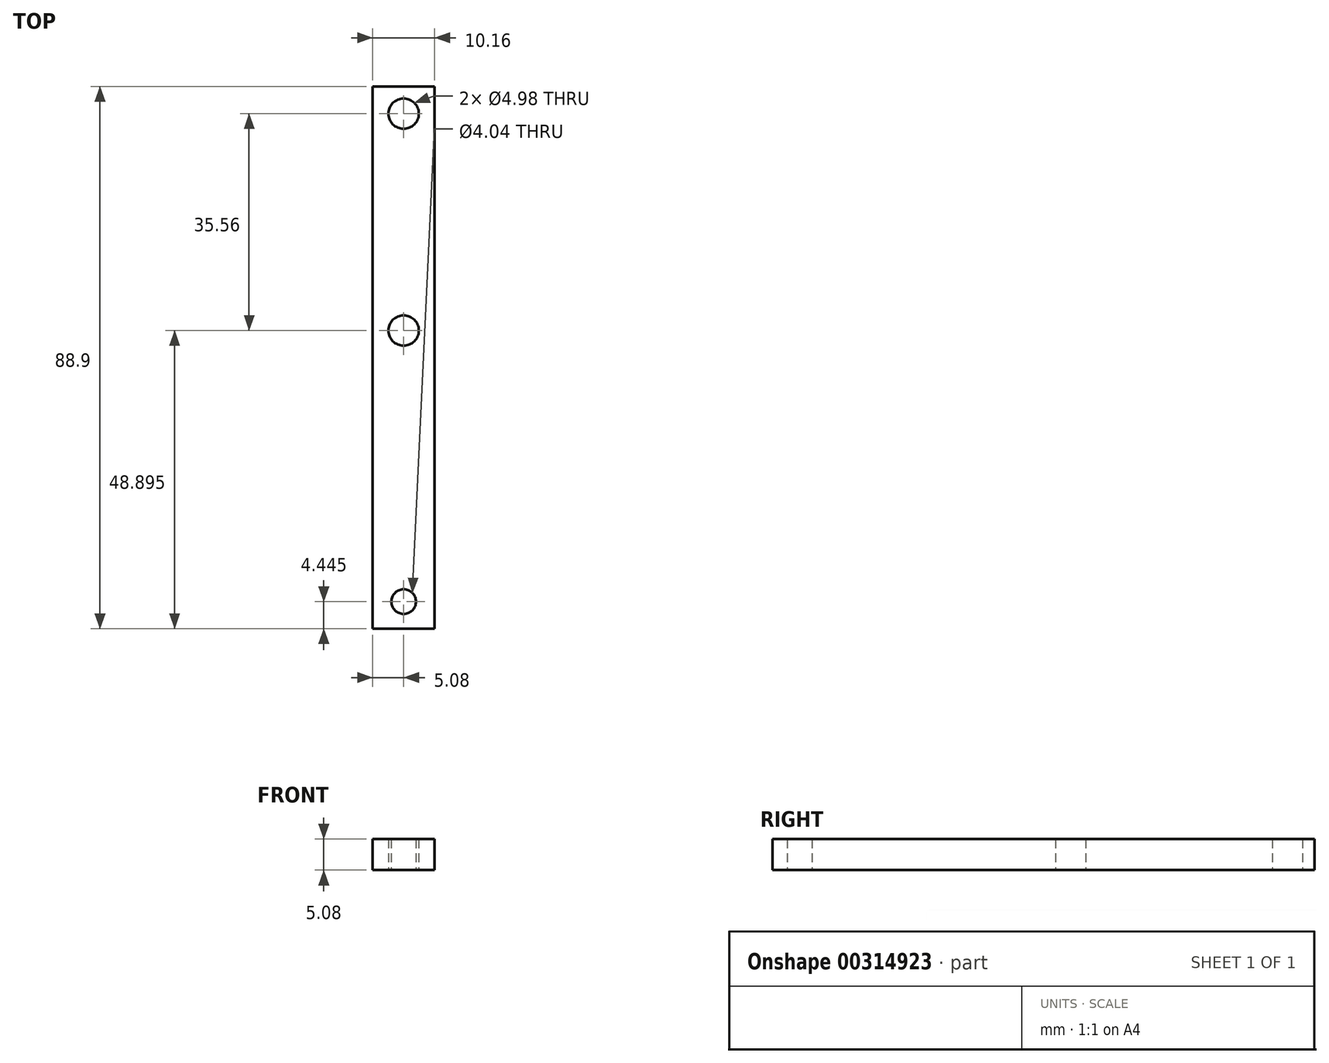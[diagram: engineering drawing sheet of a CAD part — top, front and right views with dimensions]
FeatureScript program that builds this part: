
annotation { "Feature Type Name" : "Feature", "Feature Type Description" : "" }
export const myFeature = defineFeature(function(context is Context, id is Id, definition is map)
    precondition{}
    {
        {
            var Q0;
            Q0=qCreatedBy(makeId("Top.planeOp"),FACE);
            var sketch = newSketch(context, id + "F0", { "sketchPlane" : qUnion([Q0])});
            skLineSegment(sketch, "E0.bottom", {"start": v(0, 0) * mm, "end": v(10.16, 0) * mm});
            skLineSegment(sketch, "E0.top", {"start": v(0, 88.9) * mm, "end": v(10.16, 88.9) * mm});
            skLineSegment(sketch, "E0.left", {"start": v(0, 0) * mm, "end": v(0, 88.9) * mm});
            skLineSegment(sketch, "E0.right", {"start": v(10.16, 0) * mm, "end": v(10.16, 88.9) * mm});
            skCircle(sketch, "E1", {"center": v(5.08, 48.9) * mm, "radius": 2.49 * mm});
            skCircle(sketch, "E2", {"center": v(5.08, 84.45) * mm, "radius": 2.49 * mm});
            skPoint(sketch, "E3", {"position": v(5.08, 88.9) * mm});
            skCircle(sketch, "E4", {"center": v(5.08, 4.45) * mm, "radius": 2.02 * mm});
            skSolve(sketch);
        }
        {
            var Q0;
            Q0 = qSketchRegion(id + "F0", true);
            extrude(context, id + "F1", {"entities" : qUnion([Q0]), "depth" : 5.08 * mm});
        }
    });
